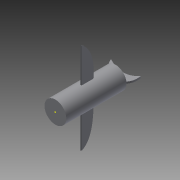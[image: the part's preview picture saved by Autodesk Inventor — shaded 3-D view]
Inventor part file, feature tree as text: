
AUTODESK INVENTOR PART (.ipt)
format: ipt  version: 2015 SP1 (Build 190203100, 203)  size: 146,944 bytes
history: native  units: in
note: dims shown in document units (in); Inventor stores cm internally (conversion verified against a paired STEP export)
features: sketch x4, extrude x3, chamfer x2, fillet x2
ambient origin geometry x8: Origin, YZ Plane, XZ Plane, XY Plane, X Axis, Y Axis, Z Axis, Center Point
bodies: Solid1 (feature_tree)
feature tree (11):
  extrude  "Extrusion1"  Depth=8.6in TaperAngle=0.0deg
  extrude  "Extrusion2"  Depth=5.0in
  chamfer  "Chamfer1"  Distance=0.125in
  chamfer  "Chamfer2"  Distance=0.125in Angle=45.0deg
  extrude  "Extrusion3"  Depth=0.125in
  fillet  "Fillet1"  Radius=0.25in
  fillet  "Fillet2"  Radius=0.125in
  sketch  "Sketch4"  dims[d11=0.125in d12=0.125in d13=45.0deg d14=1.675in d15=0.25in d16=0.0in d17=0.125in d18=0.125in]
  sketch  "Sketch1"  dims[d0=3.109in d1=8.6in d2=0.0in]
  sketch  "Sketch2"  dims[d3=1.75in d4=5.0in]
  sketch  "Sketch3"  dims[d5=5.0in d6=0.125in d7=0.0in d8=0.125in d9=0.125in d10=45.0deg]
